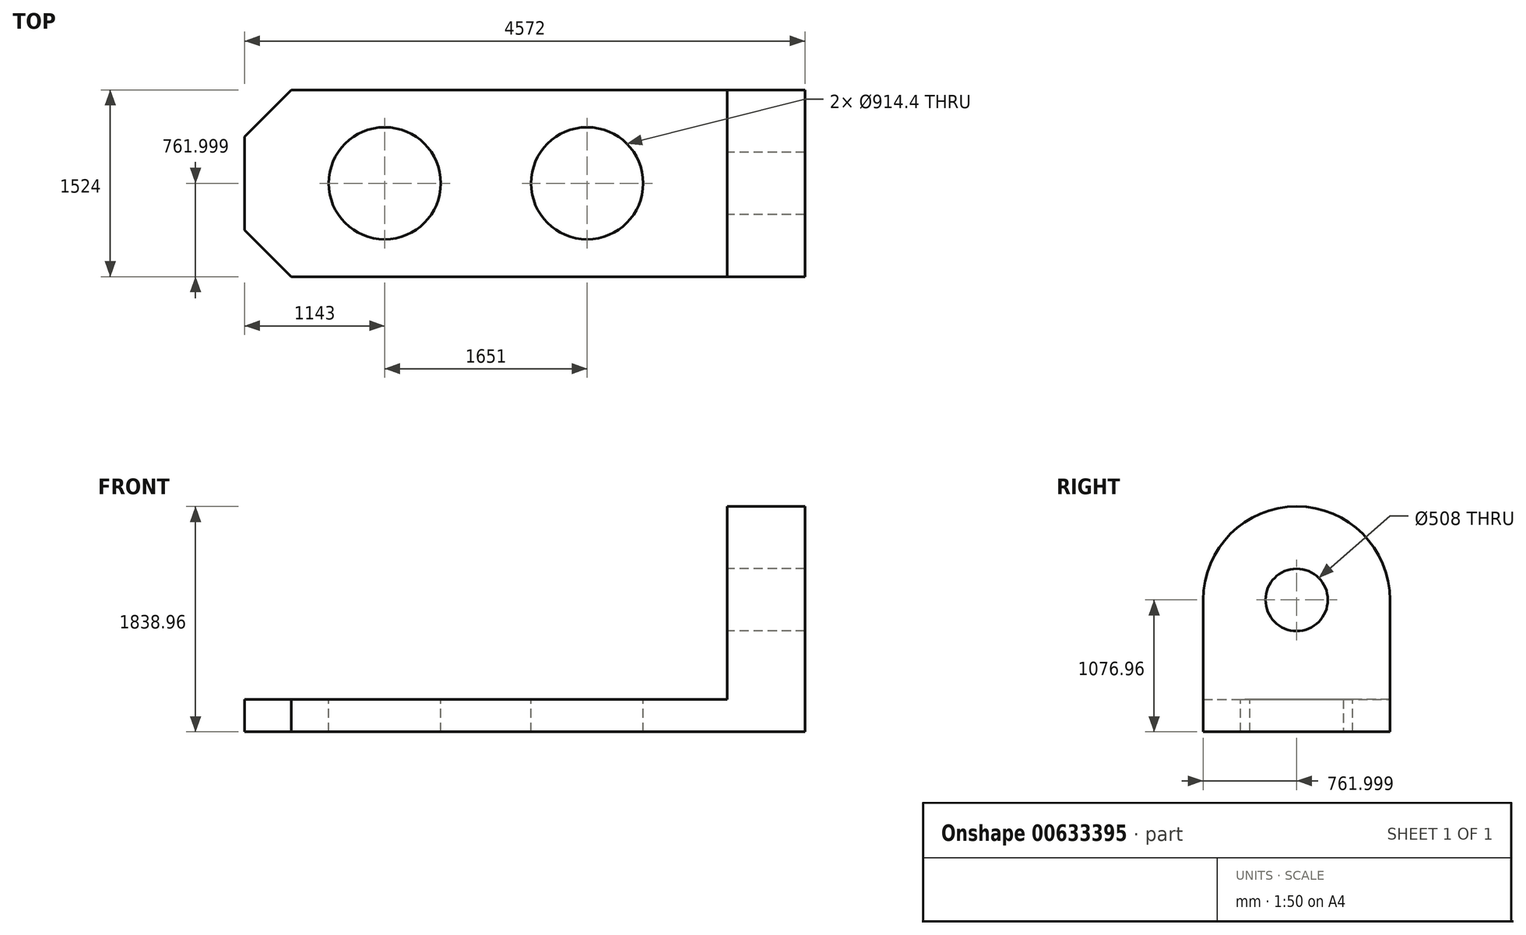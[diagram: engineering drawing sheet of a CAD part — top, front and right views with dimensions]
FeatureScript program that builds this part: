
annotation { "Feature Type Name" : "Feature", "Feature Type Description" : "" }
export const myFeature = defineFeature(function(context is Context, id is Id, definition is map)
    precondition{}
    {
        {
            var Q0;
            Q0=qCreatedBy(makeId("Top.planeOp"),FACE);
            var sketch = newSketch(context, id + "F0", { "sketchPlane" : qUnion([Q0])});
            skLineSegment(sketch, "E0.bottom", {"start": v(-2284.06, 737.37) * mm, "end": v(2287.94, 737.37) * mm});
            skLineSegment(sketch, "E0.top", {"start": v(-2284.06, -786.63) * mm, "end": v(2287.94, -786.63) * mm});
            skLineSegment(sketch, "E0.left", {"start": v(-2284.06, 737.37) * mm, "end": v(-2284.06, -786.63) * mm});
            skLineSegment(sketch, "E0.right", {"start": v(2287.94, 737.37) * mm, "end": v(2287.94, -786.63) * mm});
            skSolve(sketch);
        }
        {
            var Q0;
            Q0=makeQuery(id+"F0.imprint","IMPRINT",FACE,{"disambiguationData":[TD([[makeQuery(id+"F0.imprint","IMPRINT",EDGE,{"derivedFrom":sQuery(id+"F0.wireOp",EDGE,"E0.bottom")}),-1.0]])]});
            extrude(context, id + "F1", {"entities" : qUnion([Q0]), "depth" : 264.16 * mm, "offsetDistance" : 25.4 * mm});
        }
        {
            var Q0;
            Q0=makeQuery(id+"F1.opExtrude","CAP_FACE",FACE,{"disambiguationData":[OSD([sQuery(id+"F0.wireOp",EDGE,"E0.bottom"),sQuery(id+"F0.wireOp",EDGE,"E0.top"),sQuery(id+"F0.wireOp",EDGE,"E0.left"),sQuery(id+"F0.wireOp",EDGE,"E0.right")])],"isStart":false});
            var sketch = newSketch(context, id + "F2", { "sketchPlane" : qUnion([Q0])});
            skLineSegment(sketch, "E1.bottom", {"start": v(2287.94, -786.63) * mm, "end": v(1652.94, -786.63) * mm});
            skLineSegment(sketch, "E1.top", {"start": v(2287.94, 737.37) * mm, "end": v(1652.94, 737.37) * mm});
            skLineSegment(sketch, "E1.left", {"start": v(2287.94, -786.63) * mm, "end": v(2287.94, 737.37) * mm});
            skLineSegment(sketch, "E1.right", {"start": v(1652.94, -786.63) * mm, "end": v(1652.94, 737.37) * mm});
            skSolve(sketch);
        }
        {
            var Q0;
            Q0=makeQuery(id+"F2.imprint","IMPRINT",FACE,{"disambiguationData":[TD([[makeQuery(id+"F2.imprint","IMPRINT",EDGE,{"derivedFrom":sQuery(id+"F2.wireOp",EDGE,"E1.bottom")}),1.0]])]});
            extrude(context, id + "F3", {"entities" : qUnion([Q0]), "operationType" : NewBodyOperationType.ADD, "depth" : 1574.8 * mm, "offsetDistance" : 25.4 * mm});
        }
        {
            var Q0;
            Q0=makeQuery(id+"F3.opExtrude","CAP_EDGE",EDGE,{"disambiguationData":[OSD([sQuery(id+"F2.wireOp",EDGE,"E1.top")])],"isStart":false});
            var Q1;
            Q1=makeQuery(id+"F3.opExtrude","CAP_EDGE",EDGE,{"disambiguationData":[OSD([sQuery(id+"F2.wireOp",EDGE,"E1.bottom")])],"isStart":false});
            fillet(context, id + "F4", {"entities" : qUnion([Q0, Q1]), "radius" : 762 * mm, "tangentPropagation" : true, "allowEdgeOverflow" : false});
        }
        {
            var Q0;
            Q0=makeQuery(id+"F1.opExtrude","CAP_FACE",FACE,{"disambiguationData":[OSD([sQuery(id+"F0.wireOp",EDGE,"E0.bottom"),sQuery(id+"F0.wireOp",EDGE,"E0.top"),sQuery(id+"F0.wireOp",EDGE,"E0.left"),sQuery(id+"F0.wireOp",EDGE,"E0.right")])],"isStart":false});
            var sketch = newSketch(context, id + "F5", { "sketchPlane" : qUnion([Q0])});
            skCircle(sketch, "E2", {"center": v(509.94, -24.63) * mm, "radius": 457.2 * mm});
            skCircle(sketch, "E3", {"center": v(-1141.06, -24.63) * mm, "radius": 457.2 * mm});
            skSolve(sketch);
        }
        {
            var Q0;
            Q0=makeQuery(id+"F5.imprint","IMPRINT",FACE,{"disambiguationData":[TD([[makeQuery(id+"F5.imprint","IMPRINT",EDGE,{"derivedFrom":sQuery(id+"F5.wireOp",EDGE,"E2")}),1.0]])]});
            var Q1;
            Q1=makeQuery(id+"F5.imprint","IMPRINT",FACE,{"disambiguationData":[TD([[makeQuery(id+"F5.imprint","IMPRINT",EDGE,{"derivedFrom":sQuery(id+"F5.wireOp",EDGE,"E3")}),1.0]])]});
            extrude(context, id + "F6", {"entities" : qUnion([Q0, Q1]), "operationType" : NewBodyOperationType.REMOVE, "oppositeDirection" : true, "depth" : 1475.74 * mm, "offsetDistance" : 25.4 * mm});
        }
        {
            var Q0;
            Q0=makeQuery(id+"F3.opExtrude","SWEPT_FACE",FACE,{"disambiguationData":[OSD([sQuery(id+"F2.wireOp",EDGE,"E1.right")])]});
            var sketch = newSketch(context, id + "F7", { "sketchPlane" : qUnion([Q0])});
            skCircle(sketch, "E4", {"center": v(24.63, 1076.96) * mm, "radius": 254 * mm});
            skSolve(sketch);
        }
        {
            var Q0;
            Q0=makeQuery(id+"F7.imprint","IMPRINT",FACE,{"disambiguationData":[TD([[makeQuery(id+"F7.imprint","IMPRINT",EDGE,{"derivedFrom":sQuery(id+"F7.wireOp",EDGE,"E4")}),1.0]])]});
            extrude(context, id + "F8", {"entities" : qUnion([Q0]), "operationType" : NewBodyOperationType.REMOVE, "oppositeDirection" : true, "depth" : 863.6 * mm, "offsetDistance" : 25.4 * mm});
        }
        {
            var Q0;
            Q0=makeQuery(id+"F1.opExtrude","SWEPT_EDGE",EDGE,{"disambiguationData":[OSD([sQuery(id+"F0.wireOp",EDGE,"E0.bottom"),sQuery(id+"F0.wireOp",EDGE,"E0.left")])]});
            chamfer(context, id + "F9", {"entities" : qUnion([Q0]), "width" : 381 * mm, "tangentPropagation" : true});
        }
        {
            var Q0;
            Q0=makeQuery(id+"F1.opExtrude","SWEPT_EDGE",EDGE,{"disambiguationData":[OSD([sQuery(id+"F0.wireOp",EDGE,"E0.top"),sQuery(id+"F0.wireOp",EDGE,"E0.left")])]});
            chamfer(context, id + "F10", {"entities" : qUnion([Q0]), "width" : 381 * mm, "tangentPropagation" : true});
        }
    });
